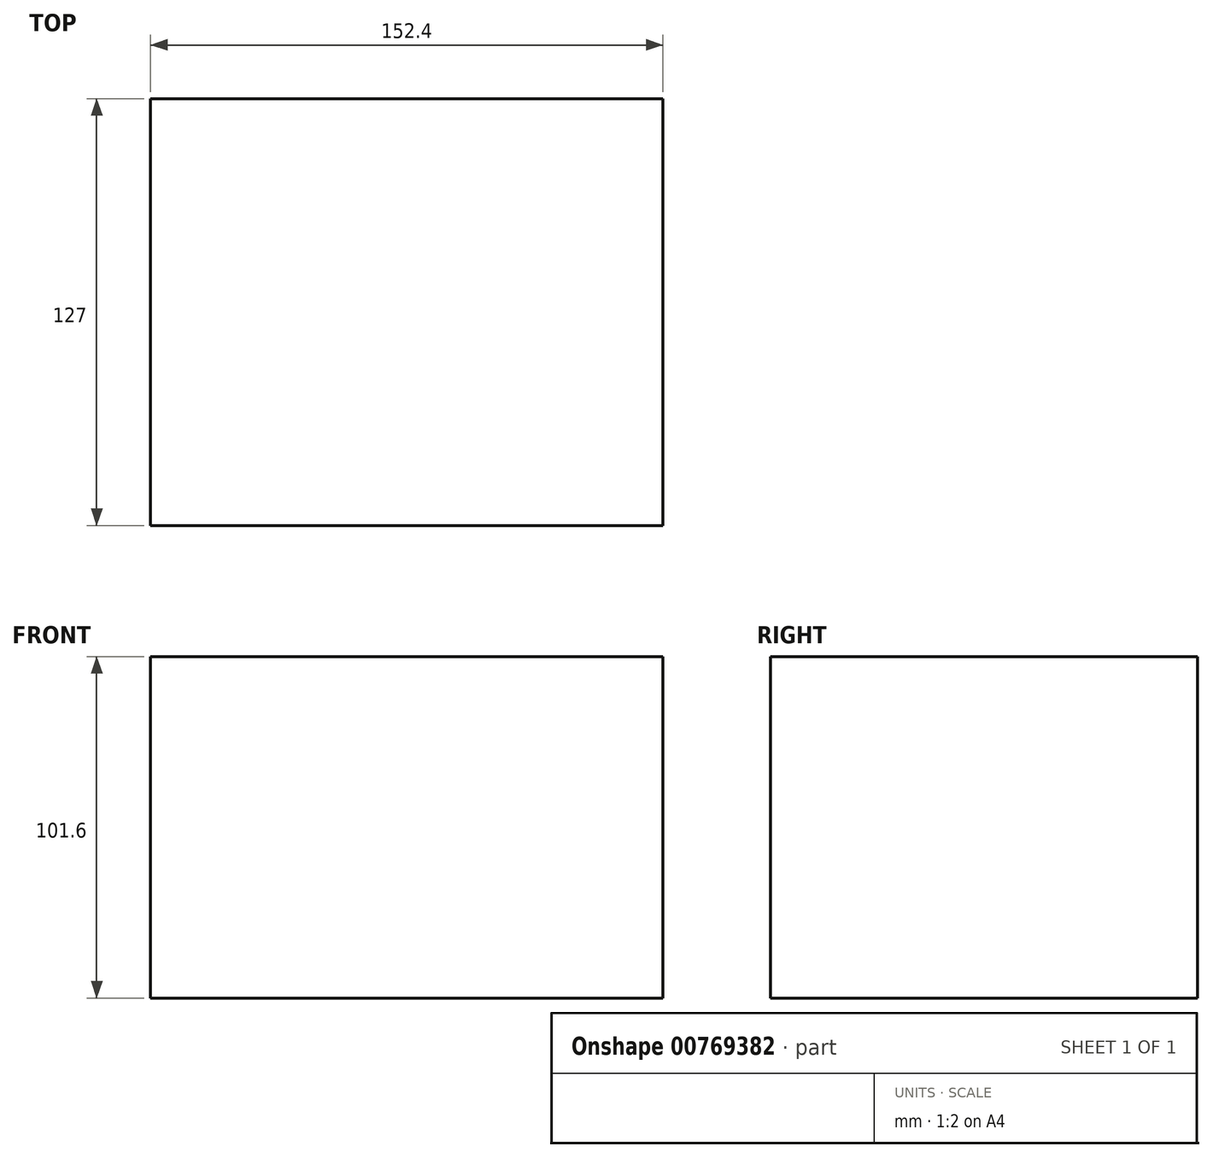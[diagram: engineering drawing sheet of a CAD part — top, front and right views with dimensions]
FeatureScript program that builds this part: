
annotation { "Feature Type Name" : "Feature", "Feature Type Description" : "" }
export const myFeature = defineFeature(function(context is Context, id is Id, definition is map)
    precondition{}
    {
        {
            var Q0;
            Q0=qCreatedBy(makeId("Front.planeOp"),FACE);
            var sketch = newSketch(context, id + "F0", { "sketchPlane" : qUnion([Q0])});
            skLineSegment(sketch, "E0", {"start": v(-80.43, -75.11) * mm, "end": v(71.97, -75.11) * mm});
            skLineSegment(sketch, "E1", {"start": v(71.97, -75.11) * mm, "end": v(71.97, 26.49) * mm});
            skLineSegment(sketch, "E2", {"start": v(71.97, 26.49) * mm, "end": v(-80.43, 26.49) * mm});
            skLineSegment(sketch, "E3", {"start": v(-80.43, 26.49) * mm, "end": v(-80.43, -75.11) * mm});
            skSolve(sketch);
        }
        {
            var Q0;
            Q0=makeQuery(id+"F0.imprint","IMPRINT",FACE,{"disambiguationData":[TD([[makeQuery(id+"F0.imprint","IMPRINT",EDGE,{"derivedFrom":sQuery(id+"F0.wireOp",EDGE,"E0")}),1.0]])]});
            extrude(context, id + "F1", {"entities" : qUnion([Q0]), "depth" : 127 * mm, "offsetDistance" : 25.4 * mm});
        }
    });
